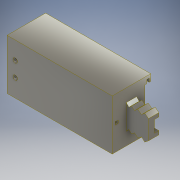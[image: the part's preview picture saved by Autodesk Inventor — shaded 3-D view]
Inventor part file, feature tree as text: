
AUTODESK INVENTOR PART (.ipt)
format: ipt  version: 2018 (Build 220112000, 112)  size: 463,360 bytes
history: native  units: mm
features: extrude x8, sketch x8, projected_geometry x3, mirror x2, other x2, plane x1, reference x1
ambient origin geometry x8: Origin, YZ Plane, XZ Plane, XY Plane, X Axis, Y Axis, Z Axis, Center Point
bodies: 实体1 (feature_tree)
feature tree (25):
  extrude  "拉伸1"  Depth=15.0mm
  extrude  "拉伸2"  Depth=67.0mm
  extrude  "拉伸3"  Depth=26.0mm TaperAngle=0.0deg
  mirror  "镜像1"
  extrude  "拉伸4"  Depth=1.5mm
  plane  "工作平面1"
  mirror  "镜像2"
  extrude  "拉伸5"  Depth=15.0mm
  extrude  "拉伸6"  Depth=65.0mm TaperAngle=0.0deg
  extrude  "拉伸7"  Depth=9.5mm TaperAngle=0.0deg
  extrude  "拉伸8"  Depth=8.0mm
  sketch  "草图1"  dims[d1=6.5mm d2=15.0mm]
  sketch  "草图2"  dims[d3=17.280505mm d4=67.0mm]
  projected_geometry  "投影回路2"
  sketch  "草图3"  dims[d6=17.0mm d7=26.0mm d8=0.0mm]
  sketch  "草图4"  dims[d9=20.0mm d11=1.5mm]
  projected_geometry  "投影回路3"
  sketch  "草图5"  dims[d12=1.5mm d13=15.0mm]
  sketch  "草图6"  dims[d14=2.0mm d15=65.0mm d16=0.0mm]
  projected_geometry  "投影回路4"
  reference  "参考1"
  sketch  "草图7"  dims[d17=4.0mm d18=0.0mm d19=9.5mm d20=0.0mm]
  sketch  "草图8"  dims[d21=9.5mm d22=0.0mm d23=8.0mm d24=3.0mm d25=68.25mm d26=0.0mm d27=3.0mm d28=3.0mm d29=10.0mm d30=1.5mm d31=9.25mm d32=0.0mm d33=2.0mm d34=2.0mm d35=2.0mm d36=5.0mm d37=0.0mm]
  other  "LED组装.iam"
  other  "转动部分:1"
